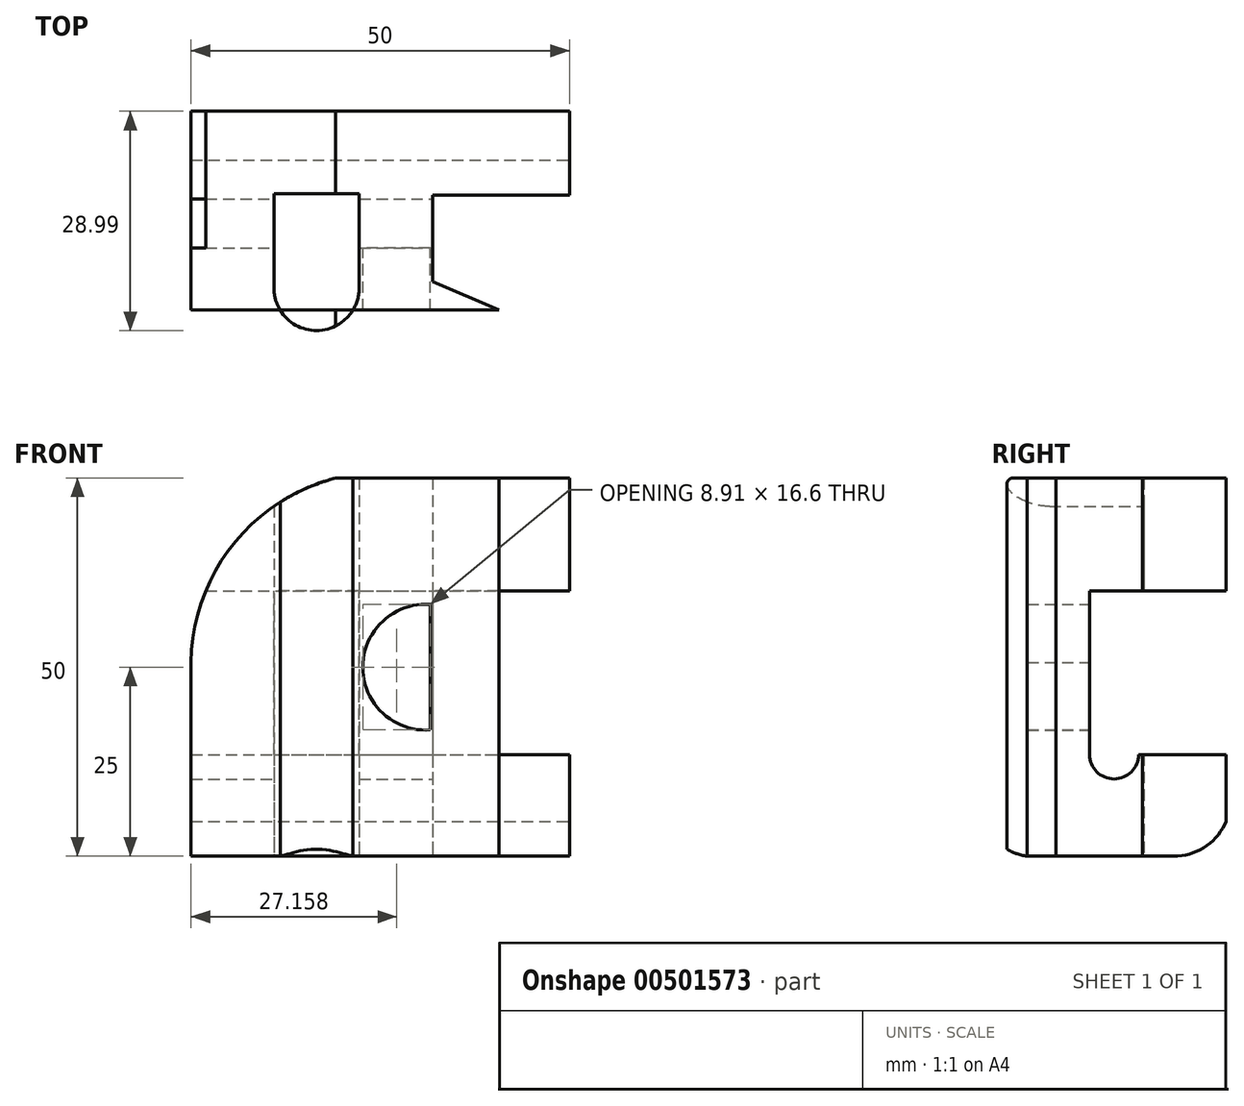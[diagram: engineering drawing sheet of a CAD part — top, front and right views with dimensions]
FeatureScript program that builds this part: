
annotation { "Feature Type Name" : "Feature", "Feature Type Description" : "" }
export const myFeature = defineFeature(function(context is Context, id is Id, definition is map)
    precondition{}
    {
        {
            var Q0;
            Q0=qCreatedBy(makeId("Top.planeOp"),FACE);
            var sketch = newSketch(context, id + "F0", { "sketchPlane" : qUnion([Q0])});
            skLineSegment(sketch, "E0.bottom", {"start": v(25, -25) * mm, "end": v(-25, -25) * mm});
            skLineSegment(sketch, "E0.top", {"start": v(25, 25) * mm, "end": v(-25, 25) * mm});
            skLineSegment(sketch, "E0.left", {"start": v(25, -25) * mm, "end": v(25, 25) * mm});
            skLineSegment(sketch, "E0.right", {"start": v(-25, -25) * mm, "end": v(-25, 25) * mm});
            skPoint(sketch, "E0.middle", {"position": v(0, 0) * mm});
            skSolve(sketch);
        }
        {
            var Q0;
            Q0=makeQuery(id+"F0.imprint","IMPRINT",FACE,{"disambiguationData":[TD([[makeQuery(id+"F0.imprint","IMPRINT",EDGE,{"derivedFrom":sQuery(id+"F0.wireOp",EDGE,"E0.bottom")}),-1.0]])]});
            extrude(context, id + "F1", {"entities" : qUnion([Q0]), "depth" : 50 * mm});
        }
        {
            var Q0;
            Q0=makeQuery(id+"F1.opExtrude","SWEPT_FACE",FACE,{"disambiguationData":[OSD([sQuery(id+"F0.wireOp",EDGE,"E0.top")])]});
            var sketch = newSketch(context, id + "F2", { "sketchPlane" : qUnion([Q0])});
            skLineSegment(sketch, "E1", {"start": v(-6.61, 33.3) * mm, "end": v(-6.61, 16.7) * mm});
            skLineSegment(sketch, "E2", {"start": v(25, 25) * mm, "end": v(-25, 25) * mm, "construction": true});
            skPoint(sketch, "E3", {"position": v(-6.61, 25) * mm});
            skArc(sketch, "E4", {"start": v(25, 25) * mm, "mid": v(19.76, 40.8) * mm, "end": v(5.88, 50) * mm});
            skArc(sketch, "E5.MirrorCS", {"start": v(25, 25) * mm, "mid": v(19.76, 9.2) * mm, "end": v(5.88, 0) * mm});
            skArc(sketch, "E6", {"start": v(-6.61, 16.7) * mm, "mid": v(2.3, 25) * mm, "end": v(-6.61, 33.3) * mm});
            skSolve(sketch);
        }
        {
            var Q0;
            Q0=makeQuery(id+"F2.imprint","IMPRINT",FACE,{"disambiguationData":[TD([[makeQuery(id+"F2.imprint","IMPRINT",EDGE,{"derivedFrom":sQuery(id+"F2.wireOp",EDGE,"E1")}),1.0]])]});
            var Q1;
            {var subQ0=sQuery(id+"F2.wireOp",EDGE,"E4");var subQ1=sQuery(id+"F0.wireOp",EDGE,"E0.top");var subQ2=makeQuery(id+"F1.opExtrude","CAP_EDGE",EDGE,{"disambiguationData":[OSD([subQ1])],"isStart":false});var subQ3=makeQuery(id+"F2.imprint","INTERSECT",VERTEX,{"derivedFrom":[subQ2,subQ0]});Q1=makeQuery(id+"F2.imprint","IMPRINT",FACE,{"disambiguationData":[TD([[makeQuery(id+"F2.imprint","IMPRINT",EDGE,{"disambiguationData":[TD([[subQ3,1.0]])],"derivedFrom":subQ0}),-1.0]])]});}
            var Q2;
            {var subQ0=sQuery(id+"F2.wireOp",EDGE,"E5.MirrorCS");var subQ1=sQuery(id+"F0.wireOp",EDGE,"E0.top");var subQ2=makeQuery(id+"F1.opExtrude","CAP_EDGE",EDGE,{"disambiguationData":[OSD([subQ1])],"isStart":true});var subQ3=makeQuery(id+"F2.imprint","INTERSECT",VERTEX,{"derivedFrom":[subQ2,subQ0]});Q2=makeQuery(id+"F2.imprint","IMPRINT",FACE,{"disambiguationData":[TD([[makeQuery(id+"F2.imprint","IMPRINT",EDGE,{"disambiguationData":[TD([[subQ3,1.0]])],"derivedFrom":subQ0}),1.0]])]});}
            extrude(context, id + "F3", {"entities" : qUnion([Q0, Q1, Q2]), "operationType" : NewBodyOperationType.REMOVE, "endBound" : BoundingType.THROUGH_ALL, "oppositeDirection" : true, "depth" : 25 * mm});
        }
        {
            var Q0;
            Q0=makeQuery(id+"F1.opExtrude","SWEPT_FACE",FACE,{"disambiguationData":[OSD([sQuery(id+"F0.wireOp",EDGE,"E0.left")])]});
            var sketch = newSketch(context, id + "F4", { "sketchPlane" : qUnion([Q0])});
            skLineSegment(sketch, "E7.bottom", {"start": v(25, 50) * mm, "end": v(-25, 50) * mm});
            skLineSegment(sketch, "E7.top", {"start": v(25, 35.1) * mm, "end": v(-25, 35.1) * mm});
            skLineSegment(sketch, "E7.left", {"start": v(25, 50) * mm, "end": v(25, 35.1) * mm});
            skLineSegment(sketch, "E7.right", {"start": v(-25, 50) * mm, "end": v(-25, 35.1) * mm});
            skLineSegment(sketch, "E8.bottom", {"start": v(6.94, 35.1) * mm, "end": v(-6.94, 35.1) * mm});
            skLineSegment(sketch, "E8.top", {"start": v(6.94, 13.45) * mm, "end": v(-6.94, 13.45) * mm});
            skLineSegment(sketch, "E8.left", {"start": v(6.94, 35.1) * mm, "end": v(6.94, 13.45) * mm});
            skLineSegment(sketch, "E8.right", {"start": v(-6.94, 35.1) * mm, "end": v(-6.94, 13.45) * mm});
            skLineSegment(sketch, "E9", {"start": v(0, 50) * mm, "end": v(0, 0) * mm, "construction": true});
            skPoint(sketch, "E10", {"position": v(0, 13.45) * mm});
            skArc(sketch, "E11", {"start": v(6.94, 13.45) * mm, "mid": v(10.18, 10.22) * mm, "end": v(13.41, 13.45) * mm});
            skLineSegment(sketch, "E12", {"start": v(-6.94, 13.45) * mm, "end": v(-6.94, 0) * mm});
            skLineSegment(sketch, "E13", {"start": v(13.41, 13.45) * mm, "end": v(25, 13.45) * mm});
            skArc(sketch, "E14", {"start": v(18.58, 0) * mm, "mid": v(22.44, 1.4) * mm, "end": v(25, 4.63) * mm});
            skArc(sketch, "E15", {"start": v(-6.94, 4.4) * mm, "mid": v(-3.91, 0.9) * mm, "end": v(0.63, 0) * mm});
            skSolve(sketch);
        }
        {
            var Q0;
            {var subQ5=sQuery(id+"F4.wireOp",EDGE,"E8.right");Q0=makeQuery(id+"F4.imprint","IMPRINT",FACE,{"disambiguationData":[TD([[makeQuery(id+"F4.imprint","IMPRINT",EDGE,{"derivedFrom":subQ5}),-1.0]])]});}
            var Q1;
            {var subQ4=sQuery(id+"F4.wireOp",EDGE,"E8.left");Q1=makeQuery(id+"F4.imprint","IMPRINT",FACE,{"disambiguationData":[TD([[makeQuery(id+"F4.imprint","IMPRINT",EDGE,{"derivedFrom":subQ4}),1.0]])]});}
            var Q2;
            {var subQ0=sQuery(id+"F4.wireOp",EDGE,"E14");Q2=makeQuery(id+"F4.imprint","IMPRINT",FACE,{"disambiguationData":[TD([[makeQuery(id+"F4.imprint","IMPRINT",EDGE,{"derivedFrom":subQ0}),-1.0]])]});}
            var Q3;
            {var subQ0=sQuery(id+"F4.wireOp",EDGE,"E12");var subQ1=makeQuery(id+"F1.opExtrude","CAP_EDGE",EDGE,{"disambiguationData":[OSD([sQuery(id+"F0.wireOp",EDGE,"E0.left")])],"isStart":true});var subQ2=makeQuery(id+"F4.imprint","INTERSECT",VERTEX,{"derivedFrom":[subQ1,subQ0]});Q3=makeQuery(id+"F4.imprint","IMPRINT",FACE,{"disambiguationData":[TD([[makeQuery(id+"F4.imprint","IMPRINT",EDGE,{"disambiguationData":[TD([[subQ2,1.0]])],"derivedFrom":subQ0}),1.0]])]});}
            extrude(context, id + "F5", {"entities" : qUnion([Q0, Q1, Q2, Q3]), "operationType" : NewBodyOperationType.REMOVE, "endBound" : BoundingType.THROUGH_ALL, "oppositeDirection" : true, "depth" : 25 * mm});
        }
        {
            var Q0;
            Q0=makeQuery(id+"F1.opExtrude","CAP_FACE",FACE,{"disambiguationData":[OSD([sQuery(id+"F0.wireOp",EDGE,"E0.bottom"),sQuery(id+"F0.wireOp",EDGE,"E0.top"),sQuery(id+"F0.wireOp",EDGE,"E0.left"),sQuery(id+"F0.wireOp",EDGE,"E0.right")])],"isStart":true});
            var sketch = newSketch(context, id + "F6", { "sketchPlane" : qUnion([Q0])});
            skPoint(sketch, "E16.0", {"position": v(-23.05, -25) * mm});
            skPoint(sketch, "E17.0", {"position": v(25, -25) * mm});
            skLineSegment(sketch, "E18.bottom", {"start": v(-23.05, -25) * mm, "end": v(25, -25) * mm});
            skLineSegment(sketch, "E18.top", {"start": v(6.94, -13.93) * mm, "end": v(25, -13.93) * mm});
            skLineSegment(sketch, "E18.left", {"start": v(-23.05, -25) * mm, "end": v(-23.05, -13.93) * mm});
            skLineSegment(sketch, "E18.right", {"start": v(25, -25) * mm, "end": v(25, -13.93) * mm});
            skLineSegment(sketch, "E19.0", {"start": v(25, 6.94) * mm, "end": v(25, 25) * mm});
            skLineSegment(sketch, "E20.0", {"start": v(-23.05, 25) * mm, "end": v(25, 25) * mm});
            skLineSegment(sketch, "E21", {"start": v(6.94, -2.49) * mm, "end": v(25, 5.33) * mm});
            skLineSegment(sketch, "E22", {"start": v(5.44, 6.36) * mm, "end": v(25, 17.16) * mm});
            skLineSegment(sketch, "E23", {"start": v(5.44, 6.36) * mm, "end": v(4.53, 8.98) * mm});
            skLineSegment(sketch, "E24", {"start": v(-23.05, -13.93) * mm, "end": v(-23.05, 3.3) * mm});
            skArc(sketch, "E25", {"start": v(4.53, 8.98) * mm, "mid": v(-11.57, 17.38) * mm, "end": v(-23.05, 3.3) * mm});
            skLineSegment(sketch, "E26", {"start": v(-14.04, -14.1) * mm, "end": v(-2.78, -14.1) * mm});
            skLineSegment(sketch, "E27", {"start": v(-14.04, -14.1) * mm, "end": v(-14.04, -1.64) * mm});
            skLineSegment(sketch, "E28", {"start": v(-2.78, -14.1) * mm, "end": v(-2.78, -1.64) * mm});
            skArc(sketch, "E29", {"start": v(-2.78, -1.64) * mm, "mid": v(-8.41, 3.99) * mm, "end": v(-14.04, -1.64) * mm});
            skLineSegment(sketch, "E30", {"start": v(-23.05, 25) * mm, "end": v(-23.05, 3.3) * mm});
            skLineSegment(sketch, "E31", {"start": v(25, 6.94) * mm, "end": v(25, -13.93) * mm});
            skLineSegment(sketch, "E32.bottom", {"start": v(-23.05, 9.1) * mm, "end": v(-27.46, 9.1) * mm});
            skLineSegment(sketch, "E32.top", {"start": v(-23.05, -12.05) * mm, "end": v(-27.46, -12.05) * mm});
            skLineSegment(sketch, "E32.left", {"start": v(-23.05, 9.1) * mm, "end": v(-23.05, -12.05) * mm});
            skLineSegment(sketch, "E32.right", {"start": v(-27.46, 9.1) * mm, "end": v(-27.46, -12.05) * mm});
            skLineSegment(sketch, "E33", {"start": v(25, 5.33) * mm, "end": v(25, 17.16) * mm});
            skLineSegment(sketch, "E34", {"start": v(6.94, -2.49) * mm, "end": v(6.94, -13.93) * mm});
            skSolve(sketch);
        }
        {
            var Q0;
            {var subQ1=sQuery(id+"F6.wireOp",EDGE,"E18.top");var subQ3=sQuery(id+"F6.wireOp",EDGE,"E21");var subQ4=makeQuery(id+"F6.imprint","INTERSECT",VERTEX,{"derivedFrom":[subQ1,subQ3]});Q0=makeQuery(id+"F6.imprint","IMPRINT",FACE,{"disambiguationData":[TD([[makeQuery(id+"F6.imprint","IMPRINT",EDGE,{"disambiguationData":[TD([[subQ4,-1.0]])],"derivedFrom":subQ1}),1.0]])]});}
            var Q1;
            {var subQ3=sQuery(id+"F6.wireOp",EDGE,"E20.0");var subQ7=sQuery(id+"F6.wireOp",EDGE,"E22");var subQ8=makeQuery(id+"F6.imprint","INTERSECT",VERTEX,{"derivedFrom":[subQ3,subQ7]});Q1=makeQuery(id+"F6.imprint","IMPRINT",FACE,{"disambiguationData":[TD([[makeQuery(id+"F6.imprint","IMPRINT",EDGE,{"disambiguationData":[TD([[subQ8,1.0]])],"derivedFrom":subQ3}),-1.0]])]});}
            var Q2;
            Q2=makeQuery(id+"F6.imprint","IMPRINT",FACE,{"disambiguationData":[TD([[makeQuery(id+"F6.imprint","IMPRINT",EDGE,{"derivedFrom":sQuery(id+"F6.wireOp",EDGE,"E26")}),1.0]])]});
            var Q3;
            {var subQ0=sQuery(id+"F6.wireOp",EDGE,"E23");var subQ1=sQuery(id+"F6.wireOp",EDGE,"E22");var subQ2=makeQuery(id+"F6.imprint","INTERSECT",VERTEX,{"derivedFrom":[sQuery(id+"F6.wireOp",EDGE,"E18.top"),subQ1,subQ0]});Q3=makeQuery(id+"F6.imprint","IMPRINT",FACE,{"disambiguationData":[TD([[makeQuery(id+"F6.imprint","IMPRINT",EDGE,{"disambiguationData":[TD([[subQ2,-1.0]])],"derivedFrom":subQ1}),1.0]])]});}
            var Q4;
            {var subQ0=sQuery(id+"F6.wireOp",EDGE,"E30");Q4=makeQuery(id+"F6.imprint","IMPRINT",FACE,{"disambiguationData":[TD([[makeQuery(id+"F6.imprint","IMPRINT",EDGE,{"derivedFrom":subQ0}),1.0]])]});}
            var Q5;
            {var subQ0=sQuery(id+"F6.wireOp",EDGE,"E31");var subQ1=sQuery(id+"F6.wireOp",EDGE,"E21");var subQ2=makeQuery(id+"F6.imprint","INTERSECT",VERTEX,{"derivedFrom":[sQuery(id+"F6.wireOp",EDGE,"E19.0"),subQ1,subQ0]});Q5=makeQuery(id+"F6.imprint","IMPRINT",FACE,{"disambiguationData":[TD([[makeQuery(id+"F6.imprint","IMPRINT",EDGE,{"disambiguationData":[TD([[subQ2,1.0]])],"derivedFrom":subQ1}),-1.0]])]});}
            var Q6;
            {var subQ3=sQuery(id+"F6.wireOp",EDGE,"E32.bottom");Q6=makeQuery(id+"F6.imprint","IMPRINT",FACE,{"disambiguationData":[TD([[makeQuery(id+"F6.imprint","IMPRINT",EDGE,{"derivedFrom":subQ3}),1.0]])]});}
            var Q7;
            {var subQ4=sQuery(id+"F6.wireOp",EDGE,"E27");Q7=makeQuery(id+"F6.imprint","IMPRINT",FACE,{"disambiguationData":[TD([[makeQuery(id+"F6.imprint","IMPRINT",EDGE,{"derivedFrom":subQ4}),-1.0]])]});}
            var Q8;
            {var subQ0=sQuery(id+"F6.wireOp",EDGE,"E31");var subQ1=sQuery(id+"F6.wireOp",EDGE,"E19.0");var subQ2=makeQuery(id+"F6.imprint","INTERSECT",VERTEX,{"derivedFrom":[subQ1,subQ0]});Q8=makeQuery(id+"F6.imprint","IMPRINT",FACE,{"disambiguationData":[TD([[makeQuery(id+"F6.imprint","IMPRINT",EDGE,{"disambiguationData":[TD([[subQ2,-1.0]])],"derivedFrom":subQ1}),1.0]])]});}
            extrude(context, id + "F7", {"entities" : qUnion([Q0, Q1, Q2, Q3, Q4, Q5, Q6, Q7, Q8]), "operationType" : NewBodyOperationType.REMOVE, "endBound" : BoundingType.THROUGH_ALL, "oppositeDirection" : true, "depth" : 25 * mm});
        }
    });
